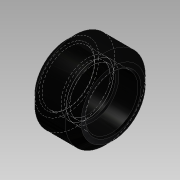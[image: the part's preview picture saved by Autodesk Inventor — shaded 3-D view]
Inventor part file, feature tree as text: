
AUTODESK INVENTOR PART (.ipt)
format: ipt  version: 2013 SP2 (Build 170200200, 200)  size: 122,880 bytes
history: native  units: mm
features: revolve x1, sketch x1
ambient origin geometry x8: Origin, YZ Plane, XZ Plane, XY Plane, X Axis, Y Axis, Z Axis, Center Point
bodies: Solid1 (feature_tree)
feature tree (2):
  revolve  "Revolution1"  [1 undecoded]
  sketch  "Sketch1"  dims[d0=5.0mm d1=20.0mm d2=90.0deg d3=8.64mm d4=15.23mm d5=0.5mm d6=3.9mm d7=12.21mm d8=9.974mm d9=135.0deg d10=0.3mm d11=0.3mm d12=5.78mm d13=90.0deg]
note: 1 required parameter value undecoded (feature->parameter linkage not recoverable at this tier; creation-order binding heuristic only, values carry confidence <= 0.55)
